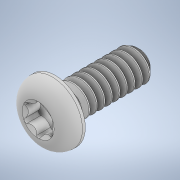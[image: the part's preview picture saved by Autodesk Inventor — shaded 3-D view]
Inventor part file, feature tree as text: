
AUTODESK INVENTOR PART (.ipt)
format: ipt  version: 2021 (Build 250183000, 183)  size: 487,936 bytes
history: native  units: in
note: dims shown in document units (in); Inventor stores cm internally (conversion verified against a paired STEP export)
features: extrude x1
ambient origin geometry x8: Origin, YZ Plane, XZ Plane, XY Plane, X Axis, Y Axis, Z Axis, Center Point
bodies: Solid1 (feature_tree)
feature tree (1):
  extrude  "Extrude16"  [1 undecoded]
note: 1 required parameter value undecoded (feature->parameter linkage not recoverable at this tier; creation-order binding heuristic only, values carry confidence <= 0.55)
